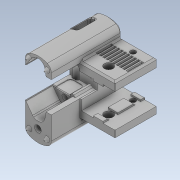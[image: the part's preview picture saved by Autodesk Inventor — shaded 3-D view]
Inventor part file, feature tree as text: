
AUTODESK INVENTOR PART (.ipt)
format: ipt  version: 2022.1 (Build 261234020, 234B)  size: 1,488,896 bytes
history: native  units: mm
features: projected_geometry x35, sketch x30, extrude x29, chamfer x20, reference x20, other x11, move_body x11, direct_edit x8, fillet x7, hole x6, plane x5, delete_face x5, mirror x1
ambient origin geometry x8: Origin, YZ Plane, XZ Plane, XY Plane, X Axis, Y Axis, Z Axis, Center Point
bodies: Volumenkörper1 (feature_tree)
feature tree (188):
  extrude  "Extrusion1"  Depth=20.0mm
  extrude  "Extrusion2"  Depth=25.0mm
  plane  "Arbeitsebene1"
  extrude  "Extrusion5"  Depth=20.0mm
  sketch  "Skizze5"  dims[d7=20.0mm d8=10.0mm]
  extrude  "Extrusion6"  Depth=10.0mm
  hole  "Bohrung1"  [1 undecoded]
  extrude  "Extrusion10"  Depth=7.1mm
  sketch  "Skizze10"  dims[d28=15.0mm d29=17.0mm]
  hole  "Bohrung2"  [1 undecoded]
  hole  "Bohrung3"  [1 undecoded]
  extrude  "Extrusion11"  Depth=0.1mm
  extrude  "Extrusion12"  Depth=7.1mm
  direct_edit  "Direktbearbeitung3"
  direct_edit  "Direktbearbeitung4"
  extrude  "Extrusion13"  Depth=7.1mm
  fillet  "Rundung6"  Radius=18.2mm
  direct_edit  "Direktbearbeitung5"
  extrude  "Extrusion14"  Depth=11.0mm TaperAngle=0.0deg
  chamfer  "Fase2"  [1 undecoded]
  chamfer  "Fase3"  [1 undecoded]
  hole  "Bohrung5"  [1 undecoded]
  extrude  "Extrusion18"  Depth=4.0mm TaperAngle=0.0deg
  chamfer  "Fase4"  Distance=11.0mm
  extrude  "Extrusion19"  TaperAngle=0.0deg  [1 undecoded]
  chamfer  "Fase5"  Distance=1.2mm
  plane  "Arbeitsebene2"
  mirror  "Spiegeln1"
  extrude  "Extrusion20"  Depth=2.0mm
  fillet  "Rundung7"  Radius=1.2mm
  extrude  "Extrusion21"  Depth=2.0mm
  chamfer  "Fase6"  Distance=1.2mm
  extrude  "Extrusion22"  Depth=2.0mm
  chamfer  "Fase7"  Distance=6.2mm
  fillet  "Rundung8"  Radius=6.2mm
  chamfer  "Fase8"  Distance=2.269mm
  chamfer  "Fase9"  Distance=10.561825mm
  extrude  "Extrusion23"  Depth=2.0mm
  extrude  "Extrusion24"  Depth=2.0mm
  direct_edit  "Direktbearbeitung6"
  direct_edit  "Direktbearbeitung7"
  chamfer  "Fase10"  Distance=0.8mm
  chamfer  "Fase11"  Distance=0.8mm
  fillet  "Rundung11"  Radius=0.8mm
  sketch  "Skizze27"  dims[d66=5.2mm d67=6.0mm d68=4.0mm d69=2.0mm d70=90.0deg d71=8.0mm d72=0.0mm]
  extrude  "Extrusion25"  Depth=2.0mm
  extrude  "Extrusion26"  Depth=2.0mm
  plane  "Arbeitsebene4"
  hole  "Bohrung6"  [1 undecoded]
  chamfer  "Fase12"  Distance=0.8mm
  direct_edit  "Direktbearbeitung8"
  plane  "Arbeitsebene3"
  extrude  "Extrusion27"  Depth=2.0mm
  extrude  "Extrusion28"  Depth=2.0mm
  chamfer  "Fase14"  Distance=6.2385mm
  chamfer  "Fase15"  Distance=8.638175mm
  chamfer  "Fase16"  Angle=90.0deg  [1 undecoded]
  extrude  "Extrusion29"  Depth=2.0mm TaperAngle=0.0deg
  delete_face  "Fläche löschen1"
  extrude  "Extrusion30"  Depth=2.0mm TaperAngle=45.0deg
  fillet  "Rundung15"  Radius=2.0mm
  extrude  "Extrusion31"  Depth=2.0mm
  delete_face  "Fläche löschen2"
  extrude  "Extrusion32"  Depth=2.0mm
  fillet  "Rundung18"  Radius=7.1mm
  chamfer  "Fase19"  Distance=1.975mm
  chamfer  "Fase20"  Distance=2.225mm
  sketch  "Skizze36"  dims[d110=1.2mm]
  extrude  "Extrusion33"  TaperAngle=0.0deg  [1 undecoded]
  extrude  "Extrusion34"  Depth=2.0mm
  extrude  "Extrusion35"  Depth=2.0mm
  delete_face  "Fläche löschen3"
  chamfer  "Fase23"  Distance=2.8mm
  chamfer  "Fase24"  Distance=2.8mm
  direct_edit  "Direktbearbeitung11"
  direct_edit  "Direktbearbeitung12"
  extrude  "Extrusion36"  Depth=2.0mm
  fillet  "Rundung20"  Radius=2.0mm
  chamfer  "Fase25"  Distance=3.6mm
  chamfer  "Fase26"  Distance=2.0mm
  delete_face  "Fläche löschen4"
  extrude  "Extrusion37"  Depth=2.0mm
  plane  "Arbeitsebene5"
  sketch  "Skizze40"  dims[d113=1.2mm d114=1.2mm d115=1.2mm d116=1.2mm d117=1.2mm d118=1.2mm d119=1.2mm d121=6.2mm d122=6.2mm d123=2.269mm d124=10.561825mm d125=10.561825mm d126=0.8mm d127=0.8mm d128=0.8mm d129=0.8mm d130=0.8mm d131=0.8mm d132=0.8mm d133=0.8mm d134=0.8mm d135=14.53mm d136=6.2385mm d137=8.638175mm d138=90.0deg d139=1.0mm d140=0.0mm d141=1.0mm d142=2.0mm d143=45.0deg d146=1.0mm d147=2.0mm d148=45.0deg d160=3.95mm d161=4.45mm d162=7.1mm d163=1.975mm d164=2.225mm d165=0.0mm d166=3.55mm d169=2.8mm d170=2.8mm d171=2.8mm d172=2.2mm d173=2.8mm d174=6.0mm d175=3.05mm d176=2.0mm d177=8.726646mm d178=7.2mm d179=0.0mm d180=2.0mm d181=3.6mm d182=2.0mm d183=3.6mm d184=4.95mm d185=0.0mm d186=0.5mm d187=2.0mm d188=45.0deg d189=5.8mm d190=25.0mm d191=12.5mm d192=0.0mm d193=1.0mm d194=0.0mm d195=1.0mm d196=2.0mm d197=45.0deg d198=5.0mm d199=0.0mm d200=0.0mm d201=1.0mm d202=1.0mm d203=0.0mm d204=1.0mm d205=2.0mm d206=45.0deg d207=135.0deg d208=0.0mm d209=0.0mm d210=1.0mm d211=2.0mm d212=45.0deg d213=5.0mm d214=1.0mm d215=2.0mm d216=45.0deg d217=0.7071mm d218=2.0mm d219=45.0deg d220=4.0mm d221=11.1mm d222=1.38mm d223=9.0mm d224=1.31mm d225=1.31mm d226=1.05mm d227=1.648525mm d228=1.0mm d229=0.0mm d230=0.0mm d231=6.5mm d232=0.0mm d233=0.0mm d234=0.0mm d235=1.0mm d236=0.0mm d237=0.0mm d238=6.0mm d239=0.6mm d240=2.0mm d241=45.0deg d242=0.6mm d243=2.0mm d244=45.0deg d247=0.5mm d248=0.01mm d249=0.01mm d250=0.07mm d251=0.07mm d252=0.1mm d253=0.1mm d254=10.0mm d255=0.0mm d256=10.0mm d257=0.0mm d259=3.3mm d260=6.0mm d261=6.5mm d262=3.4mm d263=90.0deg d264=10.1mm d265=0.0mm d266=0.4mm d267=2.0mm d268=45.0deg d269=0.0mm d270=0.0mm d271=0.5mm d273=7.24mm d274=5.8mm d275=0.72mm d276=6.8mm d279=1.0mm d280=5.8mm d281=2.0mm d282=19.02mm d283=0.0mm d288=5.0mm d289=0.0mm d290=0.0mm d291=1.0mm d292=2.0mm d293=45.0deg d294=1.0mm d295=2.0mm d296=45.0deg d297=3.0mm d298=2.0mm d299=45.0deg d300=9.71mm d301=0.0mm d302=0.0mm d303=0.0mm d304=1.0mm d305=2.0mm d306=0.0mm d315=2.2mm d316=2.2mm d317=2.0mm d318=0.0mm d319=0.4mm d339=0.4mm d340=2.0mm d341=45.0deg d342=0.4mm d343=2.0mm d344=45.0deg d345=8.6mm d346=0.1mm d348=0.1mm d349=0.1mm d350=0.1mm d351=0.1mm d352=24.0mm d353=12.0mm d354=4.2mm d355=0.0mm d356=0.0mm d357=10.0mm d358=0.0mm d359=1.8mm d360=10.0mm d361=0.0mm d368=0.4mm d369=2.0mm d370=45.0deg d371=0.4mm d372=2.0mm d373=45.0deg d374=0.0mm d375=0.0mm d376=-3.0mm d377=0.0mm d378=0.0mm d379=-3.0mm d380=0.0mm d381=0.0mm d382=-1.5mm d383=0.0mm d384=0.0mm d385=-2.5mm d386=4.7mm d387=3.828427mm d388=2.3mm d389=2.2mm d390=2.2mm d391=0.0mm d392=2.38mm d393=2.38mm d394=0.0mm d395=2.5mm d396=8.48mm d401=0.04mm d402=0.04mm d403=0.04mm d404=0.04mm d405=0.04mm d406=0.04mm d408=10.0mm d409=0.0mm d410=3.0mm d429=0.0mm d430=2.861mm d431=0.4mm d432=2.0mm d433=9.599311mm d434=0.4mm d435=2.0mm d436=9.599311mm d437=1.8mm d438=10.0mm d439=0.0mm d440=30.0mm d441=3.3mm d442=6.0mm d443=4.0mm d444=2.0mm d445=90.0deg d446=40.0mm d447=0.0mm]
  delete_face  "Fläche löschen5"
  hole  "Bohrung7"  [1 undecoded]
  sketch  "Skizze1"  dims[d0=20.0mm d1=20.0mm]
  sketch  "Skizze2"  dims[d2=21.0mm d3=25.0mm]
  sketch  "Skizze4"  dims[d4=40.0mm d5=0.0mm d6=20.0mm]
  reference  "Referenz2"
  reference  "Referenz3"
  reference  "Referenz4"
  reference  "Referenz5"
  projected_geometry  "Projizierte Kontur2"
  sketch  "Skizze6"  dims[d9=0.0mm d10=0.0mm d11=-5.0mm]
  projected_geometry  "Projizierte Kontur3"
  sketch  "Skizze8"  dims[d25=7.1mm d26=7.1mm]
  reference  "Referenz6"
  reference  "Referenz7"
  projected_geometry  "Projizierte Kontur6"
  projected_geometry  "Projizierte Kontur7"
  reference  "Referenz9"
  sketch  "Skizze11"  dims[d30=1.0mm d31=18.0mm]
  projected_geometry  "Projizierte Kontur8"
  projected_geometry  "Projizierte Kontur9"
  sketch  "Skizze12"  dims[d32=18.2mm d33=0.1mm]
  projected_geometry  "Projizierte Kontur10"
  projected_geometry  "Projizierte Kontur11"
  sketch  "Skizze13"  dims[d34=36.0mm d35=0.0mm d36=7.1mm]
  projected_geometry  "Projizierte Kontur12"
  sketch  "Skizze14"  dims[d37=3.55mm d39=7.1mm d40=18.2mm]
  projected_geometry  "Projizierte Kontur13"
  projected_geometry  "Projizierte Kontur17"
  projected_geometry  "Projizierte Kontur18"
  sketch  "Skizze20"  dims[d41=9.1mm d42=11.0mm d43=0.0mm]
  projected_geometry  "Projizierte Kontur19"
  sketch  "Skizze21"  dims[d48=3.4mm d49=6.0mm d50=4.0mm d51=2.0mm d52=90.0deg d53=8.0mm d54=0.0mm d59=0.0mm d60=0.0mm]
  projected_geometry  "Projizierte Kontur20"
  sketch  "Skizze22"  dims[d61=40.0mm]
  projected_geometry  "Projizierte Kontur21"
  sketch  "Skizze23"  dims[d62=15.5mm]
  projected_geometry  "Projizierte Kontur22"
  sketch  "Skizze24"  dims[d63=10.0mm]
  projected_geometry  "Projizierte Kontur23"
  sketch  "Skizze25"  dims[d64=6.2385mm]
  reference  "Referenz12"
  reference  "Referenz13"
  reference  "Referenz14"
  reference  "Referenz15"
  sketch  "Skizze26"  dims[d65=14.53mm]
  projected_geometry  "Projizierte Kontur24"
  projected_geometry  "Projizierte Kontur25"
  projected_geometry  "Projizierte Kontur26"
  projected_geometry  "Projizierte Kontur27"
  projected_geometry  "Projizierte Kontur28"
  sketch  "Skizze28"  dims[d73=3.2mm d74=6.0mm d75=4.0mm d76=2.0mm d77=90.0deg d78=8.0mm d79=0.0mm d80=0.0mm d81=0.0mm]
  sketch  "Skizze29"  dims[d82=11.0mm d83=0.0mm d87=0.0mm d88=0.0mm d89=4.0mm]
  projected_geometry  "Projizierte Kontur29"
  sketch  "Skizze30"  dims[d90=0.0mm d91=0.0mm d92=4.0mm d93=0.0mm d94=0.0mm d95=4.0mm]
  projected_geometry  "Projizierte Kontur30"
  projected_geometry  "Projizierte Kontur31"
  reference  "Referenz18"
  sketch  "Skizze31"  dims[d101=40.0mm]
  projected_geometry  "Projizierte Kontur32"
  projected_geometry  "Projizierte Kontur33"
  projected_geometry  "Projizierte Kontur34"
  sketch  "Skizze32"  dims[d102=20.0mm d103=11.0mm d104=0.0mm]
  projected_geometry  "Projizierte Kontur35"
  sketch  "Skizze33"  dims[d105=4.0mm d106=0.0mm d107=0.0mm d108=-5.0mm]
  projected_geometry  "Projizierte Kontur36"
  projected_geometry  "Projizierte Kontur37"
  sketch  "Skizze34"  dims[d109=9.4mm]
  projected_geometry  "Projizierte Kontur38"
  projected_geometry  "Projizierte Kontur39"
  reference  "Referenz20"
  projected_geometry  "Projizierte Kontur40"
  projected_geometry  "Projizierte Kontur41"
  sketch  "Skizze37"  dims[d111=1.2mm]
  reference  "Referenz21"
  reference  "Referenz22"
  reference  "Referenz23"
  reference  "Referenz24"
  reference  "Referenz25"
  reference  "Referenz26"
  reference  "Referenz27"
  sketch  "Skizze39"  dims[d112=1.2mm]
  other  "<userpath>\Desktop\Voron-2-2.4r1\Custom\Front_Idlers\Baugruppe1.iam"
  other  "Baugruppe1.iam"
  other  "Inside-holder:1"
  move_body  "Verschieben3"
  move_body  "Verschieben4"
  move_body  "Verschieben5"
  move_body  "Verschieben6"
  other  "<userpath>\Desktop\Voron-2-2.4r1\CAD\VORON2_v2.4_Assembly_Step\VORON2 v2.4 Assembly.iam"
  other  "VORON2 v2.4 Assembly.iam"
  other  "Z Assembly:1"
  other  "Z Belts:1"
  other  "Z Belt:2"
  move_body  "Verschieben7"
  move_body  "Verschieben8"
  move_body  "Verschieben9"
  other  "<userpath>\Desktop\Voron-2-2.4r1\Custom\Front_Idlers\Assembly_Front-Idlers2.iam"
  other  "Assembly_Front-Idlers2.iam"
  other  "Cover1:1"
  move_body  "Verschieben16"
  move_body  "Verschieben17"
  move_body  "Verschieben18"
  move_body  "Verschieben19"
note: 11 required parameter values undecoded (feature->parameter linkage not recoverable at this tier; creation-order binding heuristic only, values carry confidence <= 0.55)
